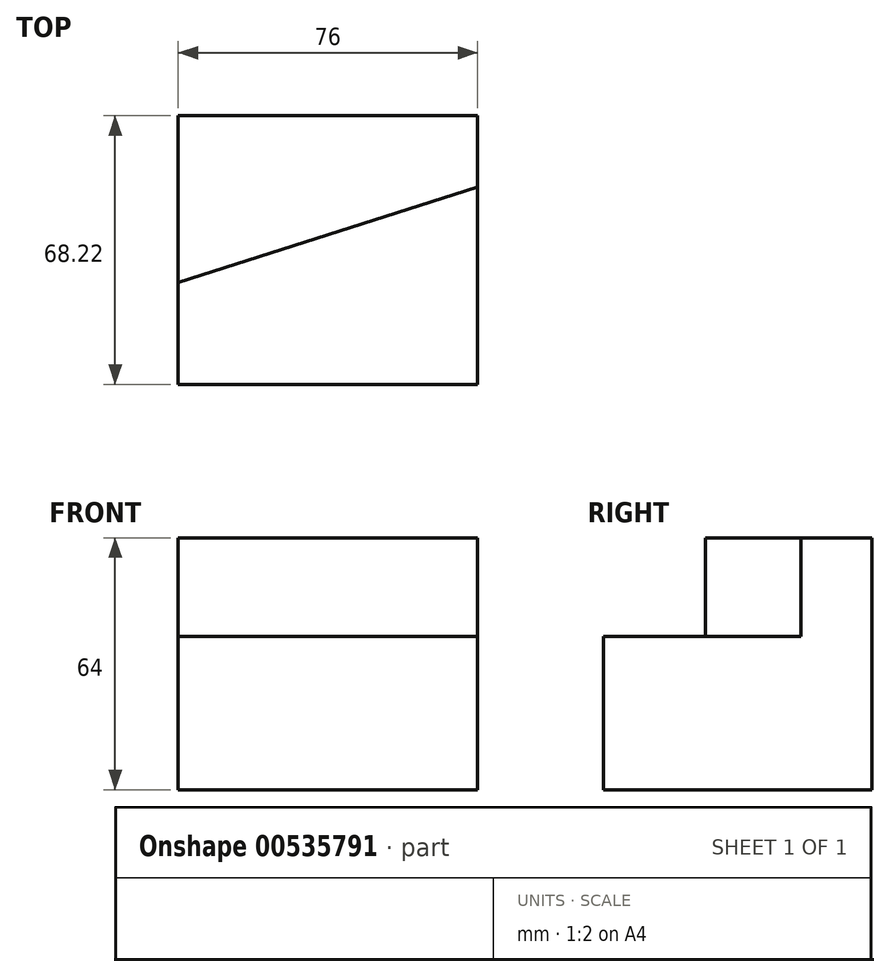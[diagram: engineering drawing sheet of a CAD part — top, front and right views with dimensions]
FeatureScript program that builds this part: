
annotation { "Feature Type Name" : "Feature", "Feature Type Description" : "" }
export const myFeature = defineFeature(function(context is Context, id is Id, definition is map)
    precondition{}
    {
        {
            var Q0;
            Q0=qCreatedBy(makeId("Top.planeOp"),FACE);
            var sketch = newSketch(context, id + "F0", { "sketchPlane" : qUnion([Q0])});
            skLineSegment(sketch, "E0.bottom", {"start": v(38, 34.1) * mm, "end": v(-38, 34.1) * mm});
            skLineSegment(sketch, "E0.top", {"start": v(38, -34.1) * mm, "end": v(-38, -34.1) * mm});
            skLineSegment(sketch, "E0.left", {"start": v(38, 34.1) * mm, "end": v(38, -34.1) * mm});
            skLineSegment(sketch, "E0.right", {"start": v(-38, 34.1) * mm, "end": v(-38, -34.1) * mm});
            skPoint(sketch, "E0.middle", {"position": v(0, 0) * mm});
            skSolve(sketch);
        }
        {
            var Q0;
            Q0=makeQuery(id+"F0.imprint","IMPRINT",FACE,{"disambiguationData":[TD([[makeQuery(id+"F0.imprint","IMPRINT",EDGE,{"derivedFrom":sQuery(id+"F0.wireOp",EDGE,"E0.bottom")}),1.0]])]});
            extrude(context, id + "F1", {"entities" : qUnion([Q0]), "endBound" : BoundingType.SYMMETRIC, "depth" : 64 * mm, "offsetDistance" : 25 * mm});
        }
        {
            var Q0;
            Q0=makeQuery(id+"F1.opExtrude","CAP_FACE",FACE,{"disambiguationData":[OSD([sQuery(id+"F0.wireOp",EDGE,"E0.bottom"),sQuery(id+"F0.wireOp",EDGE,"E0.top"),sQuery(id+"F0.wireOp",EDGE,"E0.left"),sQuery(id+"F0.wireOp",EDGE,"E0.right")])],"isStart":false});
            var sketch = newSketch(context, id + "F2", { "sketchPlane" : qUnion([Q0])});
            skLineSegment(sketch, "E1", {"start": v(38, -34.1) * mm, "end": v(38, 16.06) * mm});
            skLineSegment(sketch, "E2", {"start": v(38, 16.06) * mm, "end": v(-38, -8.22) * mm});
            skLineSegment(sketch, "E3", {"start": v(-38, -8.22) * mm, "end": v(-38, -34.1) * mm});
            skLineSegment(sketch, "E4", {"start": v(-38, -34.1) * mm, "end": v(38, -34.1) * mm});
            skSolve(sketch);
        }
        {
            var Q0;
            Q0=makeQuery(id+"F2.imprint","IMPRINT",FACE,{"disambiguationData":[TD([[makeQuery(id+"F2.imprint","IMPRINT",EDGE,{"derivedFrom":sQuery(id+"F2.wireOp",EDGE,"E1")}),-1.0]])]});
            extrude(context, id + "F3", {"entities" : qUnion([Q0]), "operationType" : NewBodyOperationType.REMOVE, "oppositeDirection" : true, "depth" : 25 * mm, "offsetDistance" : 25 * mm});
        }
    });
